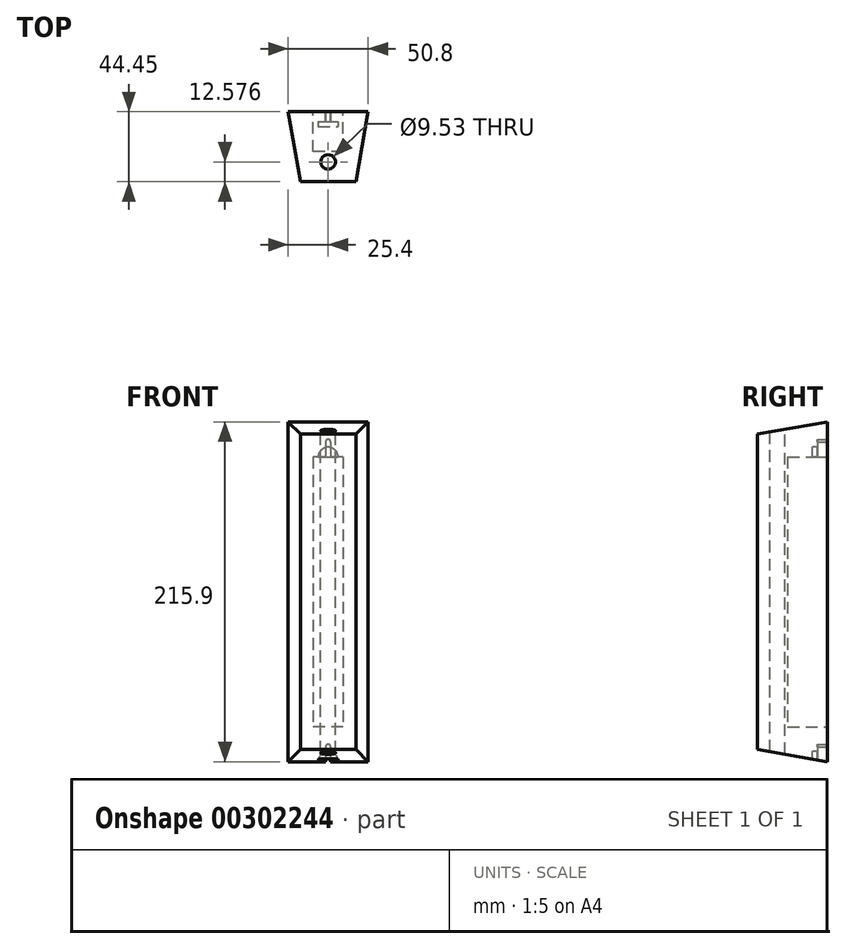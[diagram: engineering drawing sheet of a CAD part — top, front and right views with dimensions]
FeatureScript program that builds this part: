
annotation { "Feature Type Name" : "Feature", "Feature Type Description" : "" }
export const myFeature = defineFeature(function(context is Context, id is Id, definition is map)
    precondition{}
    {
        {
            var Q0;
            Q0=qCreatedBy(makeId("Front.planeOp"),FACE);
            var sketch = newSketch(context, id + "F0", { "sketchPlane" : qUnion([Q0])});
            skLineSegment(sketch, "E0.bottom", {"start": v(-25.4, 107.95) * mm, "end": v(25.4, 107.95) * mm});
            skLineSegment(sketch, "E0.top", {"start": v(-25.4, -107.95) * mm, "end": v(25.4, -107.95) * mm});
            skLineSegment(sketch, "E0.left", {"start": v(-25.4, 107.95) * mm, "end": v(-25.4, -107.95) * mm});
            skLineSegment(sketch, "E0.right", {"start": v(25.4, 107.95) * mm, "end": v(25.4, -107.95) * mm});
            skPoint(sketch, "E0.middle", {"position": v(0, 0) * mm});
            skSolve(sketch);
        }
        {
            var Q0;
            Q0 = qSketchRegion(id + "F0", true);
            extrude(context, id + "F1", {"entities" : qUnion([Q0]), "depth" : 44.45 * mm, "hasDraft" : true, "draftAngle" : 10 * degree, "draftPullDirection" : true});
        }
        {
            var Q0;
            Q0=makeQuery(id+"F1.opExtrude","CAP_FACE",FACE,{"disambiguationData":[OSD([sQuery(id+"F0.wireOp",EDGE,"E0.bottom"),sQuery(id+"F0.wireOp",EDGE,"E0.top"),sQuery(id+"F0.wireOp",EDGE,"E0.left"),sQuery(id+"F0.wireOp",EDGE,"E0.right")])],"isStart":true});
            var sketch = newSketch(context, id + "F2", { "sketchPlane" : qUnion([Q0])});
            skLineSegment(sketch, "E1.bottom", {"start": v(-9.52, 85.73) * mm, "end": v(9.53, 85.73) * mm});
            skLineSegment(sketch, "E1.top", {"start": v(-9.53, -85.73) * mm, "end": v(9.52, -85.73) * mm});
            skLineSegment(sketch, "E1.left", {"start": v(-9.52, 85.73) * mm, "end": v(-9.53, -85.73) * mm});
            skLineSegment(sketch, "E1.right", {"start": v(9.53, 85.73) * mm, "end": v(9.52, -85.73) * mm});
            skPoint(sketch, "E1.middle", {"position": v(0, 0) * mm});
            skSolve(sketch);
        }
        {
            var Q0;
            Q0 = qSketchRegion(id + "F2", true);
            extrude(context, id + "F3", {"entities" : qUnion([Q0]), "operationType" : NewBodyOperationType.REMOVE, "oppositeDirection" : true, "depth" : 25.4 * mm});
        }
        {
            var Q0;
            Q0=qCreatedBy(makeId("Top.planeOp"),FACE);
            cPlane(context, id + "F4", {"entities" : qUnion([Q0]), "cplaneType" : CPlaneType.OFFSET, "offset" : 127 * mm, "width" : 152.4 * mm, "height" : 152.4 * mm});
        }
        {
            var Q0;
            Q0=qCreatedBy(id+"F4.planeOp",FACE);
            var sketch = newSketch(context, id + "F5", { "sketchPlane" : qUnion([Q0])});
            skLineSegment(sketch, "E2", {"start": v(0, -44.57) * mm, "end": v(0, -31.87) * mm, "construction": true});
            skCircle(sketch, "E3", {"center": v(0, -31.87) * mm, "radius": 4.76 * mm});
            skSolve(sketch);
        }
        {
            var Q0;
            Q0 = qSketchRegion(id + "F5", true);
            extrude(context, id + "F6", {"entities" : qUnion([Q0]), "operationType" : NewBodyOperationType.REMOVE, "oppositeDirection" : true, "depth" : 254 * mm});
        }
        {
            var Q0;
            Q0=makeQuery(id+"F1.opExtrude","CAP_FACE",FACE,{"disambiguationData":[OSD([sQuery(id+"F0.wireOp",EDGE,"E0.bottom"),sQuery(id+"F0.wireOp",EDGE,"E0.top"),sQuery(id+"F0.wireOp",EDGE,"E0.left"),sQuery(id+"F0.wireOp",EDGE,"E0.right")])],"isStart":true});
            cPlane(context, id + "F7", {"entities" : qUnion([Q0]), "cplaneType" : CPlaneType.OFFSET, "offset" : 9.52 * mm, "oppositeDirection" : true, "width" : 152.4 * mm, "height" : 152.4 * mm});
        }
        {
            var Q0;
            Q0=qCreatedBy(id+"F7.planeOp",FACE);
            var sketch = newSketch(context, id + "F8", { "sketchPlane" : qUnion([Q0])});
            skCircle(sketch, "E4", {"center": v(0, 85.52) * mm, "radius": 6.35 * mm});
            skCircle(sketch, "E5", {"center": v(0, -107.84) * mm, "radius": 6.35 * mm});
            skSolve(sketch);
        }
        {
            var Q0;
            Q0 = qSketchRegion(id + "F8", true);
            extrude(context, id + "F9", {"entities" : qUnion([Q0]), "operationType" : NewBodyOperationType.REMOVE, "depth" : 3.17 * mm});
        }
        {
            var Q0;
            Q0=makeQuery(id+"F1.opExtrude","CAP_FACE",FACE,{"disambiguationData":[OSD([sQuery(id+"F0.wireOp",EDGE,"E0.bottom"),sQuery(id+"F0.wireOp",EDGE,"E0.top"),sQuery(id+"F0.wireOp",EDGE,"E0.left"),sQuery(id+"F0.wireOp",EDGE,"E0.right")])],"isStart":true});
            var sketch = newSketch(context, id + "F10", { "sketchPlane" : qUnion([Q0])});
            skLineSegment(sketch, "E6", {"start": v(0, 95.25) * mm, "end": v(0, 85.73) * mm, "construction": true});
            skPoint(sketch, "E7.endSnap0", {"position": v(0, -85.73) * mm});
            skLineSegment(sketch, "E8", {"start": v(0, -107.95) * mm, "end": v(0, -98.43) * mm, "construction": true});
            skPoint(sketch, "E8.endSnap0", {"position": v(0, -107.95) * mm});
            skCircle(sketch, "E9", {"center": v(0, -98.43) * mm, "radius": 1.59 * mm});
            skLineSegment(sketch, "E10", {"start": v(-1.58, -98.57) * mm, "end": v(-1.58, -107.95) * mm});
            skLineSegment(sketch, "E11", {"start": v(1.59, -98.4) * mm, "end": v(1.72, -107.95) * mm});
            skLineSegment(sketch, "E12", {"start": v(-1.58, -107.95) * mm, "end": v(1.72, -107.95) * mm});
            skCircle(sketch, "E13", {"center": v(0, 95.25) * mm, "radius": 1.59 * mm});
            skLineSegment(sketch, "E14", {"start": v(-1.59, 95.3) * mm, "end": v(-1.59, 85.73) * mm});
            skLineSegment(sketch, "E15", {"start": v(1.59, 95.26) * mm, "end": v(1.59, 85.73) * mm});
            skLineSegment(sketch, "E16", {"start": v(1.59, 85.73) * mm, "end": v(-1.59, 85.73) * mm});
            skSolve(sketch);
        }
        {
            var Q0;
            Q0 = qSketchRegion(id + "F10", true);
            extrude(context, id + "F11", {"entities" : qUnion([Q0]), "operationType" : NewBodyOperationType.REMOVE, "oppositeDirection" : true, "depth" : 6.35 * mm});
        }
    });
